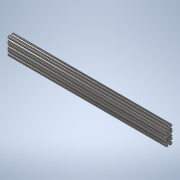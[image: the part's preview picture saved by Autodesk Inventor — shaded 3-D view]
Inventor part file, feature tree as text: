
AUTODESK INVENTOR PART (.ipt)
format: ipt  version: 2020 (Build 240168000, 168)  size: 389,120 bytes
history: native  units: in
note: dims shown in document units (in); Inventor stores cm internally (conversion verified against a paired STEP export)
features: sketch x2, extrude x1
ambient origin geometry x8: Origin, YZ Plane, XZ Plane, XY Plane, X Axis, Y Axis, Z Axis, Center Point
bodies: Solid1 (feature_tree)
feature tree (3):
  extrude  "Extrusion1"  [1 undecoded]
  sketch  "Sketch2"
  sketch  "Sketch1"  dims[d0=27.0in d1=0.0in]
note: 1 required parameter value undecoded (feature->parameter linkage not recoverable at this tier; creation-order binding heuristic only, values carry confidence <= 0.55)
